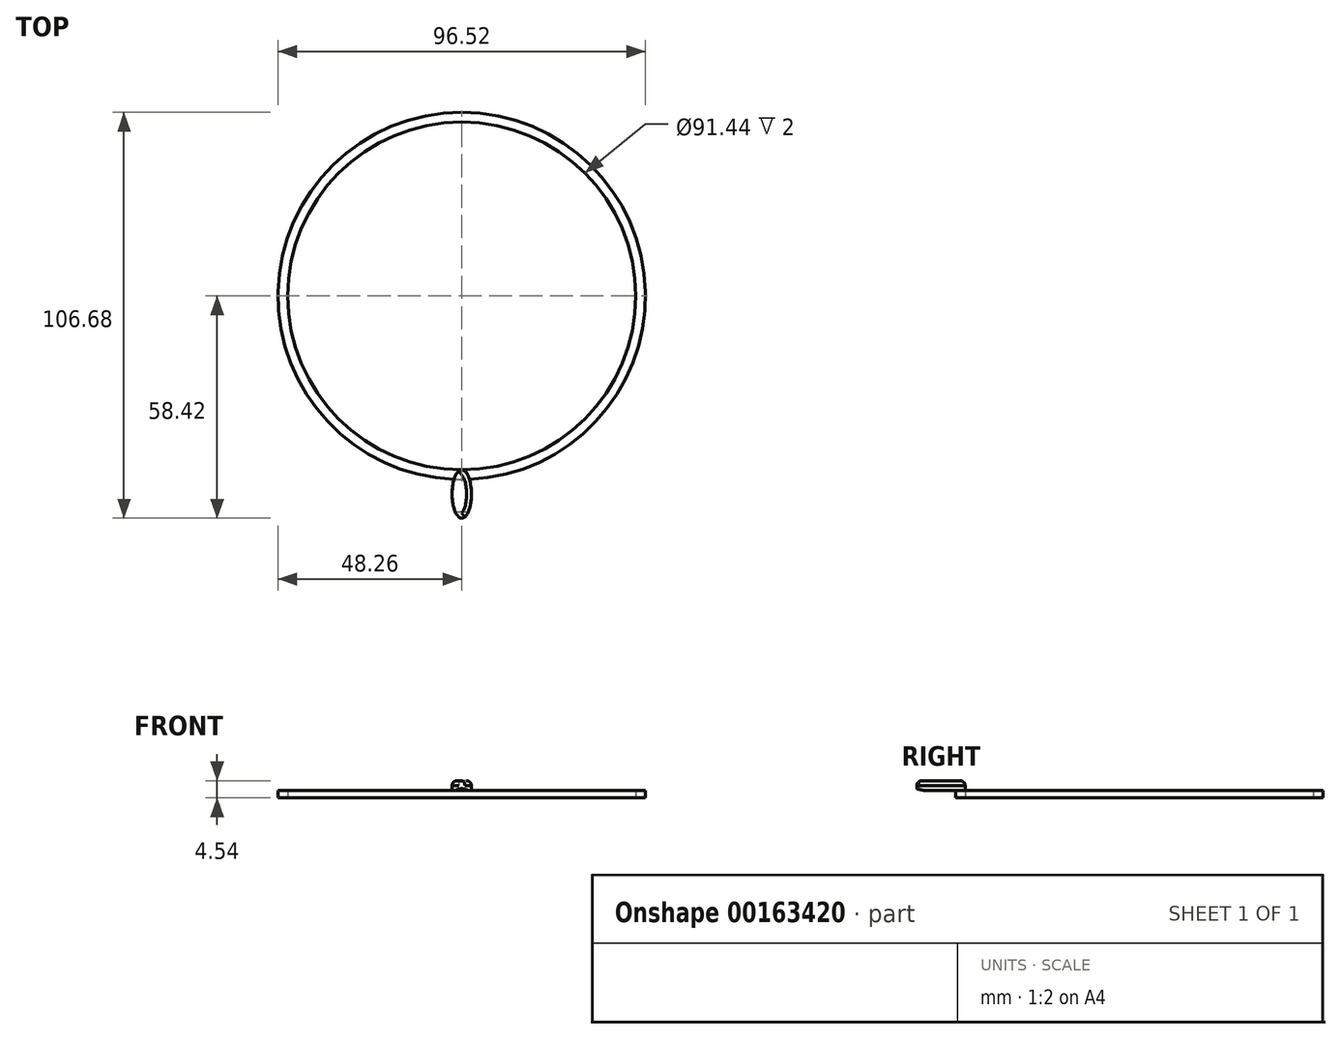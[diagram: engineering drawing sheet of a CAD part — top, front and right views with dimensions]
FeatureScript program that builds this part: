
annotation { "Feature Type Name" : "Feature", "Feature Type Description" : "" }
export const myFeature = defineFeature(function(context is Context, id is Id, definition is map)
    precondition{}
    {
        {
            var Q0;
            Q0=qCreatedBy(makeId("Top.planeOp"),FACE);
            var sketch = newSketch(context, id + "F0", { "sketchPlane" : qUnion([Q0])});
            skCircle(sketch, "E0", {"center": v(0, 0) * mm, "radius": 48.26 * mm});
            skCircle(sketch, "E1", {"center": v(0, 0) * mm, "radius": 45.72 * mm});
            skSolve(sketch);
        }
        {
            var Q0;
            Q0=makeQuery(id+"F0.imprint","IMPRINT",FACE,{"disambiguationData":[TD([[makeQuery(id+"F0.imprint","IMPRINT",EDGE,{"derivedFrom":sQuery(id+"F0.wireOp",EDGE,"E0")}),1.0]])]});
            extrude(context, id + "F1", {"entities" : qUnion([Q0]), "depth" : 2 * mm});
        }
        {
            var Q0;
            Q0=makeQuery(id+"F1.opExtrude","CAP_FACE",FACE,{"disambiguationData":[OSD([sQuery(id+"F0.wireOp",EDGE,"E0"),sQuery(id+"F0.wireOp",EDGE,"E1")])],"isStart":false});
            var sketch = newSketch(context, id + "F2", { "sketchPlane" : qUnion([Q0])});
            skLineSegment(sketch, "E2", {"start": v(0, -52.07) * mm, "end": v(0, -45.72) * mm});
            skLineSegment(sketch, "E3", {"start": v(0, -52.07) * mm, "end": v(0, -58.36) * mm});
            skEllipse(sketch, "E4", {"center": v(0, -52.07) * mm, "majorRadius": 6.35 * mm, "minorRadius": 2.54 * mm, "majorAxis": v(0, 1)});
            skSolve(sketch);
        }
        {
            var Q0;
            Q0 = qSketchRegion(id + "F2", true);
            extrude(context, id + "F3", {"entities" : qUnion([Q0]), "operationType" : NewBodyOperationType.ADD, "depth" : 2.54 * mm});
        }
        {
            var Q0;
            Q0=makeQuery(id+"F3.opExtrude","CAP_FACE",FACE,{"disambiguationData":[OSD([sQuery(id+"F2.wireOp",EDGE,"E4")])],"isStart":false});
            fillet(context, id + "F4", {"entities" : qUnion([Q0]), "radius" : 1.27 * mm, "tangentPropagation" : true, "allowEdgeOverflow" : false});
        }
        {
            var Q0;
            Q0=qCreatedBy(makeId("Right.planeOp"),FACE);
            var sketch = newSketch(context, id + "F5", { "sketchPlane" : qUnion([Q0])});
            skLineSegment(sketch, "E5", {"start": v(-58.56, 2.45) * mm, "end": v(-56.31, 1.9) * mm});
            skLineSegment(sketch, "E6", {"start": v(-56.31, 1.9) * mm, "end": v(-58.56, 1.9) * mm});
            skLineSegment(sketch, "E7", {"start": v(-58.56, 1.9) * mm, "end": v(-58.56, 2.45) * mm});
            skSolve(sketch);
        }
        {
            var Q0;
            Q0 = qSketchRegion(id + "F5", true);
            extrude(context, id + "F6", {"entities" : qUnion([Q0]), "operationType" : NewBodyOperationType.REMOVE, "oppositeDirection" : true, "depth" : 6.35 * mm, "hasSecondDirection" : true, "secondDirectionOppositeDirection" : false, "secondDirectionDepth" : 6.35 * mm});
        }
    });
